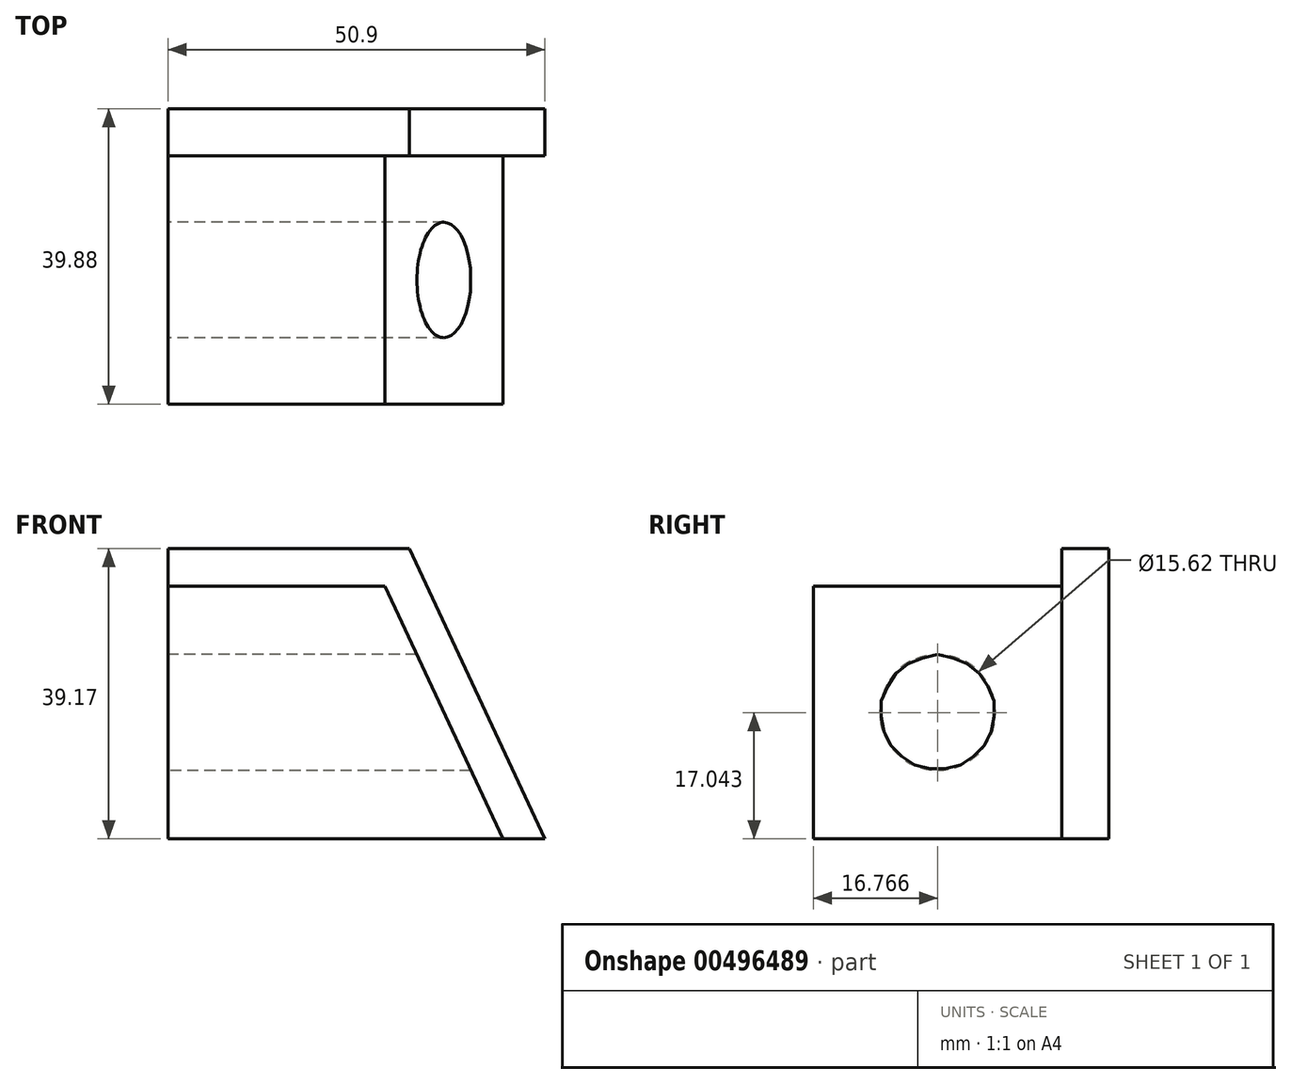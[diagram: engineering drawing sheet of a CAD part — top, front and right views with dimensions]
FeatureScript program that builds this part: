
annotation { "Feature Type Name" : "Feature", "Feature Type Description" : "" }
export const myFeature = defineFeature(function(context is Context, id is Id, definition is map)
    precondition{}
    {
        {
            var Q0;
            Q0=qCreatedBy(makeId("Front.planeOp"),FACE);
            var sketch = newSketch(context, id + "F0", { "sketchPlane" : qUnion([Q0])});
            skLineSegment(sketch, "E0", {"start": v(0, 0) * mm, "end": v(50.9, 0) * mm});
            skLineSegment(sketch, "E1", {"start": v(50.9, 0) * mm, "end": v(32.61, 39.17) * mm});
            skLineSegment(sketch, "E2", {"start": v(32.61, 39.17) * mm, "end": v(0, 39.17) * mm});
            skLineSegment(sketch, "E3", {"start": v(0, 39.17) * mm, "end": v(0, 0) * mm});
            skSolve(sketch);
        }
        {
            var Q0;
            Q0=makeQuery(id+"F0.imprint","IMPRINT",FACE,{"disambiguationData":[TD([[makeQuery(id+"F0.imprint","IMPRINT",EDGE,{"derivedFrom":sQuery(id+"F0.wireOp",EDGE,"E0")}),1.0]])]});
            extrude(context, id + "F1", {"entities" : qUnion([Q0]), "oppositeDirection" : true, "depth" : 6.35 * mm});
        }
        {
            var Q0;
            Q0=makeQuery(id+"F1.opExtrude","CAP_FACE",FACE,{"disambiguationData":[OSD([sQuery(id+"F0.wireOp",EDGE,"E0"),sQuery(id+"F0.wireOp",EDGE,"E1"),sQuery(id+"F0.wireOp",EDGE,"E2"),sQuery(id+"F0.wireOp",EDGE,"E3")])],"isStart":true});
            var sketch = newSketch(context, id + "F2", { "sketchPlane" : qUnion([Q0])});
            skLineSegment(sketch, "E4.0", {"start": v(29.3, 34.09) * mm, "end": v(0, 34.09) * mm});
            skLineSegment(sketch, "E5.0", {"start": v(45.22, 0) * mm, "end": v(29.3, 34.09) * mm});
            skSolve(sketch);
        }
        {
            var Q0;
            {var subQ0=sQuery(id+"F2.wireOp",EDGE,"E4.0");Q0=makeQuery(id+"F2.imprint","IMPRINT",FACE,{"disambiguationData":[TD([[makeQuery(id+"F2.imprint","IMPRINT",EDGE,{"derivedFrom":subQ0}),1.0]])]});}
            extrude(context, id + "F3", {"entities" : qUnion([Q0]), "operationType" : NewBodyOperationType.ADD, "depth" : 33.53 * mm});
        }
        {
            var Q0;
            {var subQ0=sQuery(id+"F0.wireOp",EDGE,"E3");Q0=makeQuery(id+"F3.boolean.opBoolean","MERGE",FACE,{"derivedFrom":[makeQuery(id+"F1.opExtrude","SWEPT_FACE",FACE,{"disambiguationData":[OSD([subQ0])]}),makeQuery(id+"F3.opExtrude","SWEPT_FACE",FACE,{"disambiguationData":[OSD([subQ0])]})]});}
            var sketch = newSketch(context, id + "F4", { "sketchPlane" : qUnion([Q0])});
            skPoint(sketch, "E6.endSnap0", {"position": v(13.59, 0) * mm});
            skCircle(sketch, "E7", {"center": v(16.76, 17.04) * mm, "radius": 7.81 * mm});
            skSolve(sketch);
        }
        {
            var Q0;
            Q0=makeQuery(id+"F4.imprint","IMPRINT",FACE,{"disambiguationData":[TD([[makeQuery(id+"F4.imprint","IMPRINT",EDGE,{"derivedFrom":sQuery(id+"F4.wireOp",EDGE,"E7")}),1.0]])]});
            extrude(context, id + "F5", {"entities" : qUnion([Q0]), "operationType" : NewBodyOperationType.REMOVE, "oppositeDirection" : true, "depth" : 76.2 * mm});
        }
    });
